# Revit family: Zumtobel MSENS HC TEC-GP WH
name_source: partatom
category: Lighting Fixtures
revit_build: Autodesk Revit 2018 (Build: 20170223_1515(x64)
units: mm (PartAtom-declared; Revit-internal decimal feet)

## family parameters
Cut with Voids When Loaded = No
Host = Face
Light Source = No
OmniClass Number = 23.80.70.11
OmniClass Title = Luminaries for Internal Lighting
Part Type = Normal
Room Calculation Point = No
Round Connector Dimension = Use Diameter
Shared = No

## types (1)
- MSENS HC TEC-GP WH
    Apparent Load = 0 VA
    Assembly Code = D5020200
    Body = ZG_Metal_White
    Default Elevation = 0 mm  [stored 0 ft]
    Depth = 90 mm  [stored 0.295276 ft]
    Description = DALI-2 Multi Sensor for motion detection and ambient light detection for connection to DALI-2 controllers.
    Height = 54 mm  [stored 0.177165 ft]
    Manufacturer = Zumtobel Lighting
    Model = 22171297
    URL = http://www.zumtobel.com
    Width = 248 mm  [stored 0.813648 ft]

note: [stored X ft] marks values corroborated as IEEE doubles in the binary element streams (Revit-internal decimal feet)

## geometry (parser evidence)
native form markers: Sweep x3
no freeform markers — native parametric forms only
